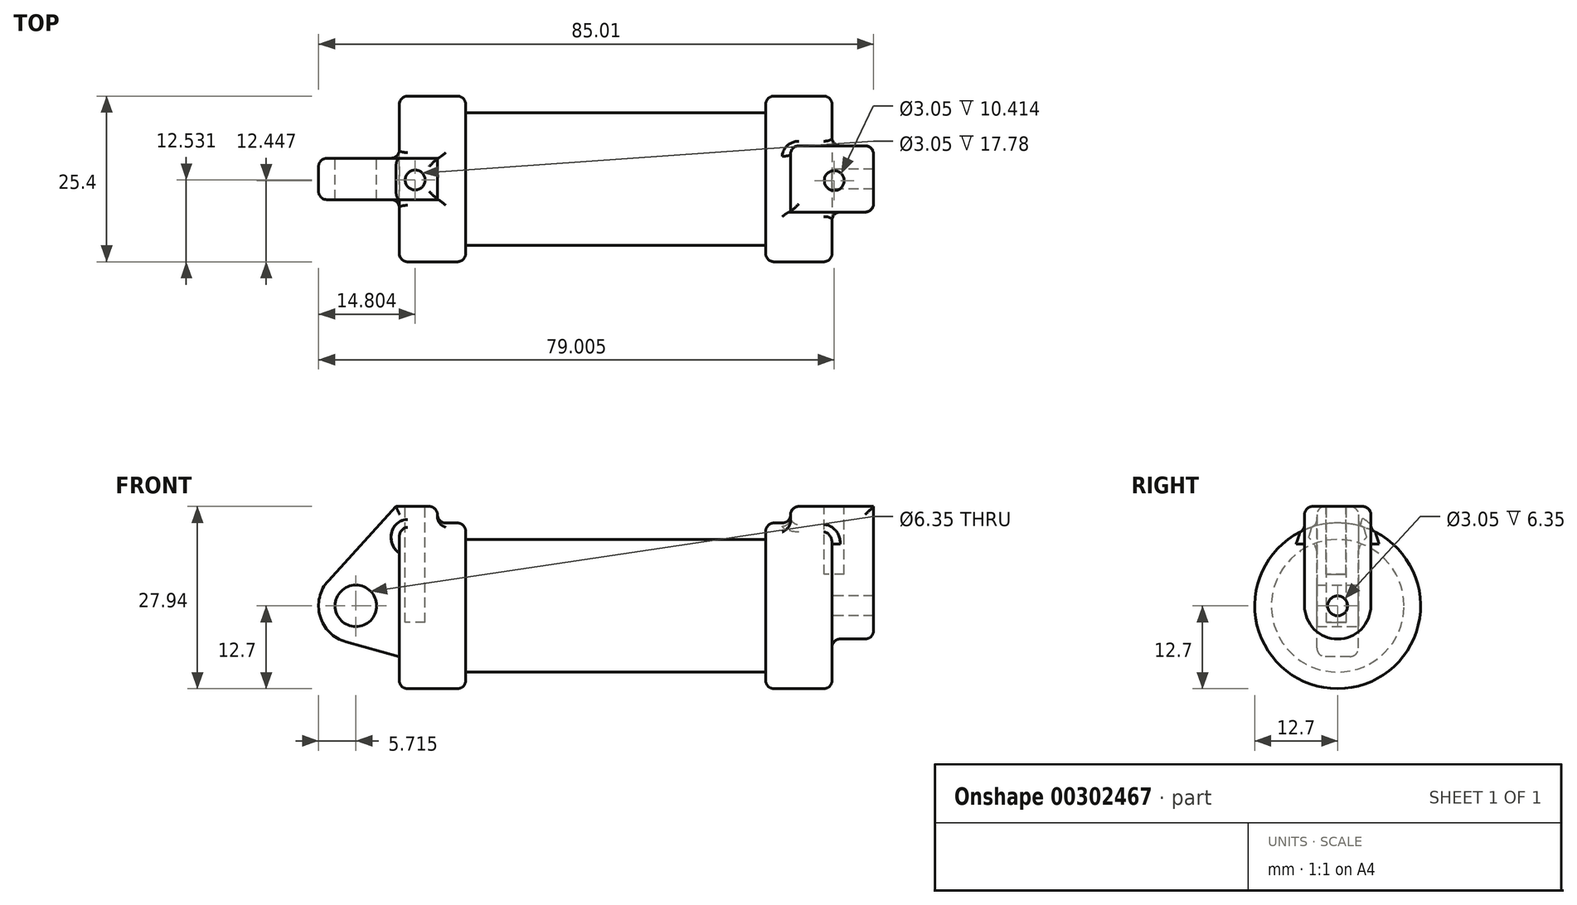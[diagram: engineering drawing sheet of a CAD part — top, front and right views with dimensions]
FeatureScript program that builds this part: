
annotation { "Feature Type Name" : "Feature", "Feature Type Description" : "" }
export const myFeature = defineFeature(function(context is Context, id is Id, definition is map)
    precondition{}
    {
        {
            var Q0;
            Q0=qCreatedBy(makeId("Front.planeOp"),FACE);
            var sketch = newSketch(context, id + "F0", { "sketchPlane" : qUnion([Q0])});
            skLineSegment(sketch, "E0", {"start": v(0, 0) * mm, "end": v(0, 12.7) * mm});
            skLineSegment(sketch, "E1", {"start": v(0, 12.7) * mm, "end": v(10.16, 12.7) * mm});
            skLineSegment(sketch, "E2", {"start": v(10.16, 12.7) * mm, "end": v(10.16, 10.16) * mm});
            skLineSegment(sketch, "E3", {"start": v(10.16, 10.16) * mm, "end": v(56.13, 10.16) * mm});
            skLineSegment(sketch, "E4", {"start": v(56.13, 10.16) * mm, "end": v(56.13, 12.7) * mm});
            skLineSegment(sketch, "E5", {"start": v(56.13, 12.7) * mm, "end": v(66.3, 12.7) * mm});
            skLineSegment(sketch, "E6", {"start": v(66.3, 12.7) * mm, "end": v(66.3, 0) * mm});
            skLineSegment(sketch, "E7", {"start": v(66.3, 0) * mm, "end": v(0, 0) * mm});
            skLineSegment(sketch, "E8", {"start": v(5.84, 15.24) * mm, "end": v(-0.5, 15.24) * mm});
            skLineSegment(sketch, "E9", {"start": v(-0.5, 15.24) * mm, "end": v(-10.88, 3.85) * mm});
            skLineSegment(sketch, "E10", {"start": v(0, 0) * mm, "end": v(-6.65, 0) * mm});
            skCircle(sketch, "E11", {"center": v(-6.65, 0) * mm, "radius": 5.72 * mm});
            skCircle(sketch, "E12", {"center": v(-6.65, 0) * mm, "radius": 3.18 * mm});
            skLineSegment(sketch, "E13", {"start": v(5.84, 15.24) * mm, "end": v(5.84, -9.4) * mm});
            skLineSegment(sketch, "E14", {"start": v(5.84, -9.4) * mm, "end": v(-8.18, -5.5) * mm});
            skSolve(sketch);
        }
        {
            var Q0;
            {var subQ0=sQuery(id+"F0.wireOp",EDGE,"E2");Q0=makeQuery(id+"F0.imprint","IMPRINT",FACE,{"disambiguationData":[TD([[makeQuery(id+"F0.imprint","IMPRINT",EDGE,{"derivedFrom":subQ0}),-1.0]])]});}
            var Q1;
            Q1=sQuery(id+"F0.wireOp",EDGE,"E7");
            revolve(context, id + "F1", {"entities" : qUnion([Q0]), "axis" : qUnion([Q1]), "revolveType" : RevolveType.FULL});
        }
        {
            var Q0;
            {var subQ1=sQuery(id+"F0.wireOp",EDGE,"E0");Q0=makeQuery(id+"F0.imprint","IMPRINT",FACE,{"disambiguationData":[TD([[makeQuery(id+"F0.imprint","IMPRINT",EDGE,{"derivedFrom":subQ1}),1.0]])]});}
            var Q1;
            {var subQ0=sQuery(id+"F0.wireOp",EDGE,"E0");Q1=makeQuery(id+"F0.imprint","IMPRINT",FACE,{"disambiguationData":[TD([[makeQuery(id+"F0.imprint","IMPRINT",EDGE,{"derivedFrom":subQ0}),-1.0]])]});}
            var Q2;
            {var subQ0=sQuery(id+"F0.wireOp",EDGE,"E14");Q2=makeQuery(id+"F0.imprint","IMPRINT",FACE,{"disambiguationData":[TD([[makeQuery(id+"F0.imprint","IMPRINT",EDGE,{"derivedFrom":subQ0}),-1.0]])]});}
            var Q3;
            {var subQ5=sQuery(id+"F0.wireOp",EDGE,"E12");Q3=makeQuery(id+"F0.imprint","IMPRINT",FACE,{"disambiguationData":[TD([[makeQuery(id+"F0.imprint","IMPRINT",EDGE,{"derivedFrom":subQ5}),-1.0]])]});}
            extrude(context, id + "F2", {"entities" : qUnion([Q0, Q1, Q2, Q3]), "operationType" : NewBodyOperationType.ADD, "endBound" : BoundingType.SYMMETRIC, "depth" : 6.35 * mm});
        }
        {
            var Q0;
            {var subQ0=sQuery(id+"F0.wireOp",EDGE,"E0");Q0=makeQuery(id+"F0.imprint","IMPRINT",FACE,{"disambiguationData":[TD([[makeQuery(id+"F0.imprint","IMPRINT",EDGE,{"derivedFrom":subQ0}),-1.0]])]});}
            var Q1;
            Q1=sQuery(id+"F0.wireOp",EDGE,"E7");
            revolve(context, id + "F3", {"operationType" : NewBodyOperationType.ADD, "entities" : qUnion([Q0]), "axis" : qUnion([Q1]), "revolveType" : RevolveType.FULL});
        }
        {
            var Q0;
            Q0=makeQuery(id+"F1.opRevolve","SWEPT_FACE",FACE,{"disambiguationData":[OSD([sQuery(id+"F0.wireOp",EDGE,"E6")])]});
            var sketch = newSketch(context, id + "F4", { "sketchPlane" : qUnion([Q0])});
            skCircle(sketch, "E15", {"center": v(0, 0) * mm, "radius": 1.52 * mm});
            skCircle(sketch, "E16", {"center": v(0, 0) * mm, "radius": 5.08 * mm});
            skLineSegment(sketch, "E17", {"start": v(-5.08, 0) * mm, "end": v(-5.08, 15.24) * mm});
            skLineSegment(sketch, "E18", {"start": v(5.08, 0) * mm, "end": v(5.08, 15.34) * mm});
            skLineSegment(sketch, "E19", {"start": v(-5.08, 15.24) * mm, "end": v(5.08, 15.24) * mm});
            skSolve(sketch);
        }
        {
            var Q0;
            Q0 = qSketchRegion(id + "F4", true);
            extrude(context, id + "F5", {"entities" : qUnion([Q0]), "operationType" : NewBodyOperationType.ADD, "endBound" : BoundingType.SYMMETRIC, "depth" : 12.7 * mm});
        }
        {
            var Q0;
            Q0=makeQuery(id+"F2.opExtrude","SWEPT_FACE",FACE,{"disambiguationData":[OSD([sQuery(id+"F0.wireOp",EDGE,"E8")])]});
            var sketch = newSketch(context, id + "F6", { "sketchPlane" : qUnion([Q0])});
            skPoint(sketch, "E20", {"position": v(2.43, -0.17) * mm});
            skCircle(sketch, "E21", {"center": v(2.43, -0.17) * mm, "radius": 1.52 * mm});
            skCircle(sketch, "E22", {"center": v(66.4, -0.06) * mm, "radius": 1.52 * mm});
            skSolve(sketch);
        }
        {
            var Q0;
            Q0=makeQuery(id+"F5.opExtrude","SWEPT_FACE",FACE,{"disambiguationData":[OSD([sQuery(id+"F4.wireOp",EDGE,"E19")])]});
            var sketch = newSketch(context, id + "F7", { "sketchPlane" : qUnion([Q0])});
            skPoint(sketch, "E23", {"position": v(66.63, -0.25) * mm});
            skCircle(sketch, "E24", {"center": v(66.63, -0.25) * mm, "radius": 1.52 * mm});
            skSolve(sketch);
        }
        {
            var Q0;
            Q0=makeQuery(id+"F7.imprint","IMPRINT",FACE,{"disambiguationData":[TD([[makeQuery(id+"F7.imprint","IMPRINT",EDGE,{"derivedFrom":sQuery(id+"F7.wireOp",EDGE,"E24")}),1.0]])]});
            extrude(context, id + "F8", {"entities" : qUnion([Q0]), "operationType" : NewBodyOperationType.REMOVE, "oppositeDirection" : true, "depth" : 10.4 * mm});
        }
        {
            var Q0;
            Q0=makeQuery(id+"F6.imprint","IMPRINT",FACE,{"disambiguationData":[TD([[makeQuery(id+"F6.imprint","IMPRINT",EDGE,{"derivedFrom":sQuery(id+"F6.wireOp",EDGE,"E21")}),1.0]])]});
            extrude(context, id + "F9", {"entities" : qUnion([Q0]), "operationType" : NewBodyOperationType.REMOVE, "oppositeDirection" : true, "depth" : 17.78 * mm});
        }
        {
            var Q0;
            Q0=makeQuery(id+"F5.opExtrude","SWEPT_EDGE",EDGE,{"disambiguationData":[OSD([sQuery(id+"F4.wireOp",EDGE,"E18"),sQuery(id+"F4.wireOp",EDGE,"E19")])]});
            var Q1;
            Q1=makeQuery(id+"F5.opExtrude","CAP_EDGE",EDGE,{"disambiguationData":[OSD([sQuery(id+"F4.wireOp",EDGE,"E18")])],"isStart":false});
            var Q2;
            Q2=makeQuery(id+"F5.boolean.opBoolean","INTERSECT",EDGE,{"derivedFrom":[makeQuery(id+"F1.opRevolve","SWEPT_FACE",FACE,{"disambiguationData":[OSD([sQuery(id+"F0.wireOp",EDGE,"E5")])]}),makeQuery(id+"F5.opExtrude","SWEPT_FACE",FACE,{"disambiguationData":[OSD([sQuery(id+"F4.wireOp",EDGE,"E18")])]})]});
            var Q3;
            Q3=makeQuery(id+"F5.opExtrude","CAP_EDGE",EDGE,{"disambiguationData":[OSD([sQuery(id+"F4.wireOp",EDGE,"E18")])],"isStart":true});
            var Q4;
            Q4=makeQuery(id+"F1.opRevolve","SWEPT_FACE",FACE,{"disambiguationData":[OSD([sQuery(id+"F0.wireOp",EDGE,"E5")])]});
            var Q5;
            Q5=makeQuery(id+"F5.opExtrude","SWEPT_FACE",FACE,{"disambiguationData":[OSD([sQuery(id+"F4.wireOp",EDGE,"E16")])]});
            var Q6;
            {var subQ0=sQuery(id+"F0.wireOp",EDGE,"E1");Q6=makeQuery(id+"F3.boolean.opBoolean","MERGE",FACE,{"derivedFrom":[makeQuery(id+"F1.opRevolve","SWEPT_FACE",FACE,{"disambiguationData":[OSD([subQ0])]}),makeQuery(id+"F3.opRevolve","SWEPT_FACE",FACE,{"disambiguationData":[OSD([subQ0])]})]});}
            var Q7;
            Q7=makeQuery(id+"F2.opExtrude","CAP_EDGE",EDGE,{"disambiguationData":[OSD([sQuery(id+"F0.wireOp",EDGE,"E8")])],"isStart":true});
            var Q8;
            Q8=makeQuery(id+"F2.opExtrude","CAP_EDGE",EDGE,{"disambiguationData":[OSD([sQuery(id+"F0.wireOp",EDGE,"E9")])],"isStart":true});
            var Q9;
            Q9=makeQuery(id+"F2.opExtrude","CAP_EDGE",EDGE,{"disambiguationData":[OSD([sQuery(id+"F0.wireOp",EDGE,"E11")])],"isStart":true});
            var Q10;
            Q10=makeQuery(id+"F2.opExtrude","CAP_EDGE",EDGE,{"disambiguationData":[OSD([sQuery(id+"F0.wireOp",EDGE,"E14")])],"isStart":true});
            var Q11;
            Q11=makeQuery(id+"F3.opRevolve","SWEPT_EDGE",EDGE,{"disambiguationData":[OSD([sQuery(id+"F0.wireOp",EDGE,"E0"),sQuery(id+"F0.wireOp",EDGE,"E1")])]});
            var Q12;
            Q12=makeQuery(id+"F1.opRevolve","SWEPT_EDGE",EDGE,{"disambiguationData":[OSD([sQuery(id+"F0.wireOp",EDGE,"E1"),sQuery(id+"F0.wireOp",EDGE,"E2")])]});
            var Q13;
            Q13=makeQuery(id+"F1.opRevolve","SWEPT_EDGE",EDGE,{"disambiguationData":[OSD([sQuery(id+"F0.wireOp",EDGE,"E5"),sQuery(id+"F0.wireOp",EDGE,"E6")])]});
            var Q14;
            Q14=makeQuery(id+"F5.opExtrude","SWEPT_EDGE",EDGE,{"disambiguationData":[OSD([sQuery(id+"F4.wireOp",EDGE,"E17"),sQuery(id+"F4.wireOp",EDGE,"E19")])]});
            var Q15;
            Q15=makeQuery(id+"F5.opExtrude","CAP_EDGE",EDGE,{"disambiguationData":[OSD([sQuery(id+"F4.wireOp",EDGE,"E19")])],"isStart":true});
            var Q16;
            Q16=makeQuery(id+"F2.opExtrude","CAP_EDGE",EDGE,{"disambiguationData":[OSD([sQuery(id+"F0.wireOp",EDGE,"E8")])],"isStart":false});
            var Q17;
            Q17=makeQuery(id+"F2.opExtrude","SWEPT_EDGE",EDGE,{"disambiguationData":[OSD([sQuery(id+"F0.wireOp",EDGE,"E8"),sQuery(id+"F0.wireOp",EDGE,"E13")])]});
            var Q18;
            Q18=makeQuery(id+"F2.opExtrude","CAP_EDGE",EDGE,{"disambiguationData":[OSD([sQuery(id+"F0.wireOp",EDGE,"E9")])],"isStart":false});
            var Q19;
            Q19=makeQuery(id+"F2.opExtrude","SWEPT_EDGE",EDGE,{"disambiguationData":[OSD([sQuery(id+"F0.wireOp",EDGE,"E9"),sQuery(id+"F0.wireOp",EDGE,"E11")])]});
            var Q20;
            Q20=makeQuery(id+"F2.opExtrude","CAP_EDGE",EDGE,{"disambiguationData":[OSD([sQuery(id+"F0.wireOp",EDGE,"E11")])],"isStart":false});
            var Q21;
            Q21=makeQuery(id+"F2.opExtrude","SWEPT_FACE",FACE,{"disambiguationData":[OSD([sQuery(id+"F0.wireOp",EDGE,"E11")])]});
            fillet(context, id + "F10", {"entities" : qUnion([Q0, Q1, Q2, Q3, Q4, Q5, Q6, Q7, Q8, Q9, Q10, Q11, Q12, Q13, Q14, Q15, Q16, Q17, Q18, Q19, Q20, Q21]), "radius" : 1.27 * mm, "tangentPropagation" : true, "allowEdgeOverflow" : false});
        }
    });
